annotation { "Feature Type Name" : "Feature", "Feature Type Description" : "" }
export const myFeature = defineFeature(function(context is Context, id is Id, definition is map)
    precondition{}
    {
        {
            var Q0;
            Q0=qCreatedBy(makeId("Front.planeOp"),FACE);
            var sketch = newSketch(context, id + "F0", { "sketchPlane" : qUnion([Q0])});
            skLineSegment(sketch, "E0.bottom", {"start": v(0, 0) * mm, "end": v(609.6, 0) * mm});
            skLineSegment(sketch, "E0.top", {"start": v(0, 101.6) * mm, "end": v(609.6, 101.6) * mm});
            skLineSegment(sketch, "E0.left", {"start": v(0, 0) * mm, "end": v(0, 101.6) * mm});
            skLineSegment(sketch, "E0.right", {"start": v(609.6, 0) * mm, "end": v(609.6, 101.6) * mm});
            skPoint(sketch, "E1.oppositeSnap0", {"position": v(304.8, 0) * mm});
            skSolve(sketch);
        }
        {
            var Q0;
            Q0=makeQuery(id+"F0.imprint","IMPRINT",FACE,{"disambiguationData":[TD([[makeQuery(id+"F0.imprint","IMPRINT",EDGE,{"derivedFrom":sQuery(id+"F0.wireOp",EDGE,"E0.bottom")}),1.0]])]});
            extrude(context, id + "F1", {"entities" : qUnion([Q0]), "oppositeDirection" : true, "depth" : 1.27 * mm});
        }
        {
            var Q0;
            Q0=makeQuery(id+"F1.opExtrude","CAP_FACE",FACE,{"disambiguationData":[OSD([sQuery(id+"F0.wireOp",EDGE,"E0.bottom"),sQuery(id+"F0.wireOp",EDGE,"E0.top"),sQuery(id+"F0.wireOp",EDGE,"E0.left"),sQuery(id+"F0.wireOp",EDGE,"E0.right")])],"isStart":true});
            var sketch = newSketch(context, id + "F2", { "sketchPlane" : qUnion([Q0])});
            skCircle(sketch, "E2", {"center": v(31.75, 31.75) * mm, "radius": 7.14 * mm, "construction": true});
            skCircle(sketch, "E3.1.0.0", {"center": v(88.9, 31.75) * mm, "radius": 7.14 * mm, "construction": true});
            skCircle(sketch, "E3.2.0.0", {"center": v(146.05, 31.75) * mm, "radius": 7.14 * mm, "construction": true});
            skCircle(sketch, "E3.3.0.0", {"center": v(203.2, 31.75) * mm, "radius": 7.14 * mm, "construction": true});
            skCircle(sketch, "E3.4.0.0", {"center": v(260.35, 31.75) * mm, "radius": 7.14 * mm, "construction": true});
            skCircle(sketch, "E3.5.0.0", {"center": v(317.5, 31.75) * mm, "radius": 7.14 * mm, "construction": true});
            skCircle(sketch, "E3.6.0.0", {"center": v(374.65, 31.75) * mm, "radius": 7.14 * mm, "construction": true});
            skCircle(sketch, "E3.7.0.0", {"center": v(431.8, 31.75) * mm, "radius": 7.14 * mm, "construction": true});
            skLineSegment(sketch, "E3.direction1", {"start": v(31.75, 31.75) * mm, "end": v(88.9, 31.75) * mm, "construction": true});
            skSolve(sketch);
        }
        {
            var Q0;
            Q0=makeQuery(id+"F2.imprint","IMPRINT",FACE,{"disambiguationData":[TD([[makeQuery(id+"F2.imprint","IMPRINT",EDGE,{"derivedFrom":makeQuery(id+"F1.opExtrude","CAP_EDGE",EDGE,{"disambiguationData":[OSD([sQuery(id+"F0.wireOp",EDGE,"E0.bottom")])],"isStart":true})}),1.0]])]});
            var sketch = newSketch(context, id + "F3", { "sketchPlane" : qUnion([Q0])});
            skText(sketch, "E4", { "text": "VALVE 1", "fontName": "AllertaStencil-Regular.ttf"});
            const initialGuessF3  = {"E4": [0.00927, 0.00318, 1, 0, 0.00762]};
            skSetInitialGuess(sketch, initialGuessF3);
            skSolve(sketch);
        }
        {
            var Q0;
            Q0 = qSketchRegion(id + "F3", true);
            extrude(context, id + "F4", {"entities" : qUnion([Q0]), "operationType" : NewBodyOperationType.REMOVE, "endBound" : BoundingType.THROUGH_ALL, "oppositeDirection" : true, "depth" : 25.4 * mm});
        }
        {
            var Q0;
            Q0=makeQuery(id+"F2.imprint","IMPRINT",FACE,{"disambiguationData":[TD([[makeQuery(id+"F2.imprint","IMPRINT",EDGE,{"derivedFrom":makeQuery(id+"F1.opExtrude","CAP_EDGE",EDGE,{"disambiguationData":[OSD([sQuery(id+"F0.wireOp",EDGE,"E0.bottom")])],"isStart":true})}),1.0]])]});
            var sketch = newSketch(context, id + "F5", { "sketchPlane" : qUnion([Q0])});
            skText(sketch, "E5", { "text": "VALVE 2", "fontName": "AllertaStencil-Regular.ttf"});
            const initialGuessF5  = {"E5": [0.0654, 0.00317, 1, 0, 0.00762]};
            skSetInitialGuess(sketch, initialGuessF5);
            skSolve(sketch);
        }
        {
            var Q0;
            Q0 = qSketchRegion(id + "F5", true);
            extrude(context, id + "F6", {"entities" : qUnion([Q0]), "operationType" : NewBodyOperationType.REMOVE, "endBound" : BoundingType.THROUGH_ALL, "oppositeDirection" : true, "depth" : 25.4 * mm});
        }
        {
            var Q0;
            Q0=makeQuery(id+"F2.imprint","IMPRINT",FACE,{"disambiguationData":[TD([[makeQuery(id+"F2.imprint","IMPRINT",EDGE,{"derivedFrom":makeQuery(id+"F1.opExtrude","CAP_EDGE",EDGE,{"disambiguationData":[OSD([sQuery(id+"F0.wireOp",EDGE,"E0.bottom")])],"isStart":true})}),1.0]])]});
            var sketch = newSketch(context, id + "F7", { "sketchPlane" : qUnion([Q0])});
            skText(sketch, "E6", { "text": "VALVE 3", "fontName": "AllertaStencil-Regular.ttf"});
            const initialGuessF7  = {"E6": [0.12258, 0.00318, 1, 0, 0.00762]};
            skSetInitialGuess(sketch, initialGuessF7);
            skSolve(sketch);
        }
        {
            var Q0;
            Q0 = qSketchRegion(id + "F7", true);
            extrude(context, id + "F8", {"entities" : qUnion([Q0]), "operationType" : NewBodyOperationType.REMOVE, "endBound" : BoundingType.THROUGH_ALL, "oppositeDirection" : true, "depth" : 25.4 * mm});
        }
        {
            var Q0;
            Q0=makeQuery(id+"F2.imprint","IMPRINT",FACE,{"disambiguationData":[TD([[makeQuery(id+"F2.imprint","IMPRINT",EDGE,{"derivedFrom":makeQuery(id+"F1.opExtrude","CAP_EDGE",EDGE,{"disambiguationData":[OSD([sQuery(id+"F0.wireOp",EDGE,"E0.bottom")])],"isStart":true})}),1.0]])]});
            var sketch = newSketch(context, id + "F9", { "sketchPlane" : qUnion([Q0])});
            skText(sketch, "E7", { "text": "VALVE 4", "fontName": "AllertaStencil-Regular.ttf"});
            const initialGuessF9  = {"E7": [0.17945, 0.00318, 1, 0, 0.00762]};
            skSetInitialGuess(sketch, initialGuessF9);
            skSolve(sketch);
        }
        {
            var Q0;
            Q0 = qSketchRegion(id + "F9", true);
            extrude(context, id + "F10", {"entities" : qUnion([Q0]), "operationType" : NewBodyOperationType.REMOVE, "endBound" : BoundingType.THROUGH_ALL, "oppositeDirection" : true, "depth" : 25.4 * mm});
        }
        {
            var Q0;
            Q0=makeQuery(id+"F2.imprint","IMPRINT",FACE,{"disambiguationData":[TD([[makeQuery(id+"F2.imprint","IMPRINT",EDGE,{"derivedFrom":makeQuery(id+"F1.opExtrude","CAP_EDGE",EDGE,{"disambiguationData":[OSD([sQuery(id+"F0.wireOp",EDGE,"E0.bottom")])],"isStart":true})}),1.0]])]});
            var sketch = newSketch(context, id + "F11", { "sketchPlane" : qUnion([Q0])});
            skText(sketch, "E8", { "text": "VALVE 5", "fontName": "AllertaStencil-Regular.ttf"});
            const initialGuessF11  = {"E8": [0.23673, 0.00317, 1, 0, 0.00762]};
            skSetInitialGuess(sketch, initialGuessF11);
            skSolve(sketch);
        }
        {
            var Q0;
            Q0 = qSketchRegion(id + "F11", true);
            extrude(context, id + "F12", {"entities" : qUnion([Q0]), "operationType" : NewBodyOperationType.REMOVE, "endBound" : BoundingType.THROUGH_ALL, "oppositeDirection" : true, "depth" : 25.4 * mm});
        }
        {
            var Q0;
            Q0=makeQuery(id+"F2.imprint","IMPRINT",FACE,{"disambiguationData":[TD([[makeQuery(id+"F2.imprint","IMPRINT",EDGE,{"derivedFrom":makeQuery(id+"F1.opExtrude","CAP_EDGE",EDGE,{"disambiguationData":[OSD([sQuery(id+"F0.wireOp",EDGE,"E0.bottom")])],"isStart":true})}),1.0]])]});
            var sketch = newSketch(context, id + "F13", { "sketchPlane" : qUnion([Q0])});
            skText(sketch, "E9", { "text": "VALVE 6", "fontName": "AllertaStencil-Regular.ttf"});
            const initialGuessF13  = {"E9": [0.29362, 0.00317, 1, 0, 0.00762]};
            skSetInitialGuess(sketch, initialGuessF13);
            skSolve(sketch);
        }
        {
            var Q0;
            Q0 = qSketchRegion(id + "F13", true);
            extrude(context, id + "F14", {"entities" : qUnion([Q0]), "operationType" : NewBodyOperationType.REMOVE, "endBound" : BoundingType.THROUGH_ALL, "oppositeDirection" : true, "depth" : 25.4 * mm});
        }
        {
            var Q0;
            Q0=makeQuery(id+"F2.imprint","IMPRINT",FACE,{"disambiguationData":[TD([[makeQuery(id+"F2.imprint","IMPRINT",EDGE,{"derivedFrom":makeQuery(id+"F1.opExtrude","CAP_EDGE",EDGE,{"disambiguationData":[OSD([sQuery(id+"F0.wireOp",EDGE,"E0.bottom")])],"isStart":true})}),1.0]])]});
            var sketch = newSketch(context, id + "F15", { "sketchPlane" : qUnion([Q0])});
            skText(sketch, "E10", { "text": "VALVE 7", "fontName": "AllertaStencil-Regular.ttf"});
            const initialGuessF15  = {"E10": [0.35103, 0.00318, 1, 0, 0.00762]};
            skSetInitialGuess(sketch, initialGuessF15);
            skSolve(sketch);
        }
        {
            var Q0;
            Q0 = qSketchRegion(id + "F15", true);
            extrude(context, id + "F16", {"entities" : qUnion([Q0]), "operationType" : NewBodyOperationType.REMOVE, "endBound" : BoundingType.THROUGH_ALL, "oppositeDirection" : true, "depth" : 25.4 * mm});
        }
        {
            var Q0;
            Q0=makeQuery(id+"F2.imprint","IMPRINT",FACE,{"disambiguationData":[TD([[makeQuery(id+"F2.imprint","IMPRINT",EDGE,{"derivedFrom":makeQuery(id+"F1.opExtrude","CAP_EDGE",EDGE,{"disambiguationData":[OSD([sQuery(id+"F0.wireOp",EDGE,"E0.bottom")])],"isStart":true})}),1.0]])]});
            var sketch = newSketch(context, id + "F17", { "sketchPlane" : qUnion([Q0])});
            skText(sketch, "E11", { "text": "VALVE 8", "fontName": "AllertaStencil-Regular.ttf"});
            const initialGuessF17  = {"E11": [0.40818, 0.00318, 1, 0, 0.00762]};
            skSetInitialGuess(sketch, initialGuessF17);
            skSolve(sketch);
        }
        {
            var Q0;
            Q0 = qSketchRegion(id + "F17", true);
            extrude(context, id + "F18", {"entities" : qUnion([Q0]), "operationType" : NewBodyOperationType.REMOVE, "endBound" : BoundingType.THROUGH_ALL, "oppositeDirection" : true, "depth" : 25.4 * mm});
        }
        {
            var Q0;
            Q0=makeQuery(id+"F2.imprint","IMPRINT",FACE,{"disambiguationData":[TD([[makeQuery(id+"F2.imprint","IMPRINT",EDGE,{"derivedFrom":makeQuery(id+"F1.opExtrude","CAP_EDGE",EDGE,{"disambiguationData":[OSD([sQuery(id+"F0.wireOp",EDGE,"E0.bottom")])],"isStart":true})}),1.0]])]});
            var sketch = newSketch(context, id + "F19", { "sketchPlane" : qUnion([Q0])});
            skText(sketch, "E12", { "text": "ON", "fontName": "AllertaStencil-Regular.ttf"});
            skText(sketch, "E13", { "text": "ON\n", "fontName": "AllertaStencil-Regular.ttf"});
            skText(sketch, "E14", { "text": "ON", "fontName": "AllertaStencil-Regular.ttf"});
            skText(sketch, "E15", { "text": "ON", "fontName": "AllertaStencil-Regular.ttf"});
            skText(sketch, "E16", { "text": "ON", "fontName": "AllertaStencil-Regular.ttf"});
            skText(sketch, "E17", { "text": "ON", "fontName": "AllertaStencil-Regular.ttf"});
            skText(sketch, "E18", { "text": "ON", "fontName": "AllertaStencil-Regular.ttf"});
            skText(sketch, "E19", { "text": "ON", "fontName": "AllertaStencil-Regular.ttf"});
            const initialGuessF19  = {"E12": [0.00254, 0.01397, 1, 0, 0.00762], "E13": [0.0597, 0.01397, 1, 0, 0.00762], "E14": [0.11684, 0.01397, 1, 0, 0.00762], "E15": [0.174, 0.01397, 1, 0, 0.00762], "E16": [0.23114, 0.01397, 1, 0, 0.00762], "E17": [0.2883, 0.01397, 1, 0, 0.00762], "E18": [0.34544, 0.01397, 1, 0, 0.00762], "E19": [0.40259, 0.01397, 1, 0, 0.00762]};
            skSetInitialGuess(sketch, initialGuessF19);
            skSolve(sketch);
        }
        {
            var Q0;
            Q0 = qSketchRegion(id + "F19", true);
            extrude(context, id + "F20", {"entities" : qUnion([Q0]), "operationType" : NewBodyOperationType.REMOVE, "endBound" : BoundingType.THROUGH_ALL, "oppositeDirection" : true, "depth" : 25.4 * mm});
        }
        {
            var Q0;
            Q0=makeQuery(id+"F2.imprint","IMPRINT",FACE,{"disambiguationData":[TD([[makeQuery(id+"F2.imprint","IMPRINT",EDGE,{"derivedFrom":makeQuery(id+"F1.opExtrude","CAP_EDGE",EDGE,{"disambiguationData":[OSD([sQuery(id+"F0.wireOp",EDGE,"E0.bottom")])],"isStart":true})}),1.0]])]});
            var sketch = newSketch(context, id + "F21", { "sketchPlane" : qUnion([Q0])});
            skText(sketch, "E20", { "text": "OFF", "fontName": "AllertaStencil-Regular.ttf"});
            skText(sketch, "E21", { "text": "OFF", "fontName": "AllertaStencil-Regular.ttf"});
            skText(sketch, "E22", { "text": "OFF", "fontName": "AllertaStencil-Regular.ttf"});
            skText(sketch, "E23", { "text": "OFF", "fontName": "AllertaStencil-Regular.ttf"});
            skText(sketch, "E24", { "text": "OFF", "fontName": "AllertaStencil-Regular.ttf"});
            skText(sketch, "E25", { "text": "OFF", "fontName": "AllertaStencil-Regular.ttf"});
            skText(sketch, "E26", { "text": "OFF", "fontName": "AllertaStencil-Regular.ttf"});
            skText(sketch, "E27", { "text": "OFF", "fontName": "AllertaStencil-Regular.ttf"});
            const initialGuessF21  = {"E20": [0.00254, 0.04064, 1, 0, 0.00762], "E21": [0.05969, 0.04064, 1, 0, 0.00762], "E22": [0.11684, 0.04064, 1, 0, 0.00762], "E23": [0.174, 0.04064, 1, 0, 0.00762], "E24": [0.23114, 0.04064, 1, 0, 0.00762], "E25": [0.2883, 0.04064, 1, 0, 0.00762], "E26": [0.34544, 0.04064, 1, 0, 0.00762], "E27": [0.40259, 0.04064, 1, 0, 0.00762]};
            skSetInitialGuess(sketch, initialGuessF21);
            skSolve(sketch);
        }
        {
            var Q0;
            Q0 = qSketchRegion(id + "F21", true);
            extrude(context, id + "F22", {"entities" : qUnion([Q0]), "operationType" : NewBodyOperationType.REMOVE, "endBound" : BoundingType.THROUGH_ALL, "oppositeDirection" : true, "depth" : 25.4 * mm});
        }
        {
            var Q0;
            Q0=makeQuery(id+"F2.imprint","IMPRINT",FACE,{"disambiguationData":[TD([[makeQuery(id+"F2.imprint","IMPRINT",EDGE,{"derivedFrom":makeQuery(id+"F1.opExtrude","CAP_EDGE",EDGE,{"disambiguationData":[OSD([sQuery(id+"F0.wireOp",EDGE,"E0.bottom")])],"isStart":true})}),1.0]])]});
            var sketch = newSketch(context, id + "F23", { "sketchPlane" : qUnion([Q0])});
            skText(sketch, "E28", { "text": "ISOPROPYL", "fontName": "AllertaStencil-Regular.ttf"});
            skText(sketch, "E29", { "text": "ALCOHOL", "fontName": "AllertaStencil-Regular.ttf"});
            skText(sketch, "E30", { "text": "DENATURED", "fontName": "AllertaStencil-Regular.ttf"});
            skText(sketch, "E31", { "text": "ALCOHOL", "fontName": "AllertaStencil-Regular.ttf"});
            skText(sketch, "E32", { "text": "CALLA 1452", "fontName": "AllertaStencil-Regular.ttf"});
            skText(sketch, "E33", { "text": "COKE", "fontName": "AllertaStencil-Regular.ttf"});
            skText(sketch, "E34", { "text": "SPRITE", "fontName": "AllertaStencil-Regular.ttf"});
            skText(sketch, "E35", { "text": "COFFEE", "fontName": "AllertaStencil-Regular.ttf"});
            skText(sketch, "E36", { "text": "PROPYLENE", "fontName": "AllertaStencil-Regular.ttf"});
            skText(sketch, "E37", { "text": "GLYCOL", "fontName": "AllertaStencil-Regular.ttf"});
            const initialGuessF23  = {"E28": [0.00787, 0.09144, 1, 0, 0.00635], "E29": [0.01054, 0.08128, 1, 0, 0.00635], "E30": [0.06604, 0.09144, 1, 0, 0.00635], "E31": [0.07163, 0.08128, 1, 0, 0.00635], "E32": [0.127, 0.09144, 1, 0, 0.00635], "E33": [0.19144, 0.09144, 1, 0, 0.00635], "E34": [0.2457, 0.09144, 1, 0, 0.00635], "E35": [0.30861, 0.09144, 1, 0, 0.00635], "E36": [0.34948, 0.09144, 1, 0, 0.00635], "E37": [0.35738, 0.08128, 1, 0, 0.00635]};
            skSetInitialGuess(sketch, initialGuessF23);
            skSolve(sketch);
        }
        {
            var Q0;
            Q0 = qSketchRegion(id + "F23", true);
            extrude(context, id + "F24", {"entities" : qUnion([Q0]), "operationType" : NewBodyOperationType.REMOVE, "endBound" : BoundingType.THROUGH_ALL, "oppositeDirection" : true, "depth" : 25.4 * mm});
        }
        {
            var Q0;
            Q0=makeQuery(id+"F2.imprint","IMPRINT",FACE,{"disambiguationData":[TD([[makeQuery(id+"F2.imprint","IMPRINT",EDGE,{"derivedFrom":makeQuery(id+"F1.opExtrude","CAP_EDGE",EDGE,{"disambiguationData":[OSD([sQuery(id+"F0.wireOp",EDGE,"E0.bottom")])],"isStart":true})}),1.0]])]});
            var sketch = newSketch(context, id + "F25", { "sketchPlane" : qUnion([Q0])});
            skText(sketch, "E38", { "text": "PRESSURE GAUGE", "fontName": "AllertaStencil-Regular.ttf"});
            skText(sketch, "E39", { "text": "PRESSURE", "fontName": "AllertaStencil-Regular.ttf"});
            skText(sketch, "E40", { "text": "REGULATOR", "fontName": "AllertaStencil-Regular.ttf"});
            const initialGuessF25  = {"E38": [0.45009, 0.09144, 1, 0, 0.00762], "E39": [0.5499, 0.09144, 1, 0, 0.00762], "E40": [0.54102, 0.07874, 1, 0, 0.00762]};
            skSetInitialGuess(sketch, initialGuessF25);
            skSolve(sketch);
        }
        {
            var Q0;
            Q0 = qSketchRegion(id + "F25", true);
            extrude(context, id + "F26", {"entities" : qUnion([Q0]), "operationType" : NewBodyOperationType.REMOVE, "endBound" : BoundingType.THROUGH_ALL, "oppositeDirection" : true, "depth" : 25.4 * mm});
        }
    });